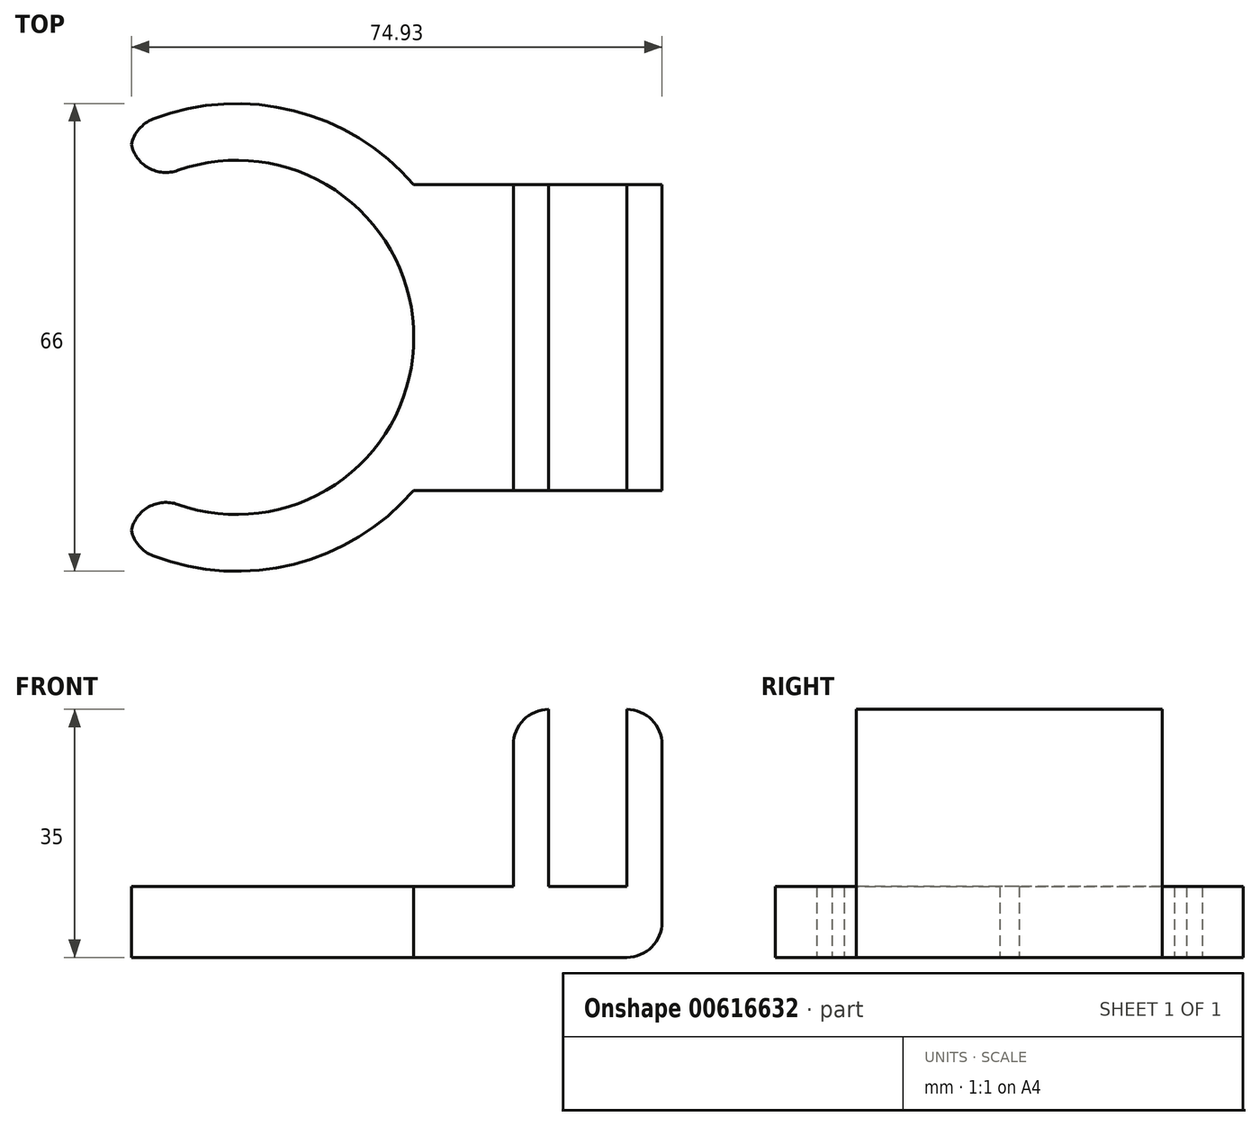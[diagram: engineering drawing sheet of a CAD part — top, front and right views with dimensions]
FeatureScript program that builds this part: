
annotation { "Feature Type Name" : "Feature", "Feature Type Description" : "" }
export const myFeature = defineFeature(function(context is Context, id is Id, definition is map)
    precondition{}
    {
        {
            var Q0;
            Q0=qCreatedBy(makeId("Top.planeOp"),FACE);
            var sketch = newSketch(context, id + "F0", { "sketchPlane" : qUnion([Q0])});
            skArc(sketch, "E0", {"start": v(-47, -20) * mm, "mid": v(-7, 0) * mm, "end": v(-47, 20) * mm});
            skArc(sketch, "E1", {"start": v(-47, -29.4) * mm, "mid": v(1, 0) * mm, "end": v(-47, 29.4) * mm});
            skLineSegment(sketch, "E2", {"start": v(-47, 29.4) * mm, "end": v(-47, 20) * mm});
            skLineSegment(sketch, "E3.trimOffspring", {"start": v(-47, -20) * mm, "end": v(-47, -29.4) * mm});
            skLineSegment(sketch, "E4.bottom", {"start": v(-7.04, 21.58) * mm, "end": v(7.04, 21.58) * mm});
            skLineSegment(sketch, "E4.top", {"start": v(-7.04, -21.58) * mm, "end": v(7.04, -21.58) * mm});
            skLineSegment(sketch, "E4.left", {"start": v(-7.04, 21.58) * mm, "end": v(-7.04, -21.58) * mm});
            skLineSegment(sketch, "E4.right", {"start": v(7.04, 21.58) * mm, "end": v(7.04, -21.58) * mm});
            skPoint(sketch, "E4.middle", {"position": v(0, 0) * mm});
            skLineSegment(sketch, "E5.bottom", {"start": v(7.04, 21.58) * mm, "end": v(12.04, 21.58) * mm});
            skLineSegment(sketch, "E5.top", {"start": v(7.04, -21.58) * mm, "end": v(12.04, -21.58) * mm});
            skLineSegment(sketch, "E5.right", {"start": v(12.04, 21.58) * mm, "end": v(12.04, -21.58) * mm});
            skLineSegment(sketch, "E6.bottom", {"start": v(12.04, 21.58) * mm, "end": v(23.04, 21.58) * mm});
            skLineSegment(sketch, "E6.top", {"start": v(12.04, -21.58) * mm, "end": v(23.04, -21.58) * mm});
            skLineSegment(sketch, "E6.right", {"start": v(23.04, 21.58) * mm, "end": v(23.04, -21.58) * mm});
            skLineSegment(sketch, "E7.bottom", {"start": v(23.04, 21.58) * mm, "end": v(28.04, 21.58) * mm});
            skLineSegment(sketch, "E7.top", {"start": v(23.04, -21.58) * mm, "end": v(28.04, -21.58) * mm});
            skLineSegment(sketch, "E7.right", {"start": v(28.04, 21.58) * mm, "end": v(28.04, -21.58) * mm});
            skSolve(sketch);
        }
        {
            var Q0;
            Q0=qSketchRegion(id+"F0",true);
            var Q1;
            {var subQ0=sQuery(id+"F0.wireOp",EDGE,"45a05517-1ebe-4f36-a2c0-a8144c21bbce1.MirrorCS");var subQ1=sQuery(id+"F0.wireOp",EDGE,"E1");var subQ2=makeQuery(id+"F0.imprint","INTERSECT",VERTEX,{"disambiguationData":[OD(0.0)],"derivedFrom":[subQ1,subQ0]});Q1=makeQuery(id+"F0.imprint","IMPRINT",FACE,{"disambiguationData":[TD([[makeQuery(id+"F0.imprint","IMPRINT",EDGE,{"disambiguationData":[TD([[subQ2,-1.0]])],"derivedFrom":subQ1}),1.0]])]});}
            extrude(context, id + "F1", {"entities" : qUnion([Q0, Q1]), "depth" : 5 * mm, "offsetDistance" : 25 * mm, "hasSecondDirection" : true, "secondDirectionOppositeDirection" : true, "secondDirectionDepth" : 5 * mm});
        }
        {
            var Q0;
            Q0=makeQuery(id+"F1.opExtrude","SWEPT_EDGE",EDGE,{"disambiguationData":[OSD([sQuery(id+"F0.wireOp",EDGE,"E0"),sQuery(id+"F0.wireOp",EDGE,"E2")])]});
            var Q1;
            Q1=makeQuery(id+"F1.opExtrude","SWEPT_EDGE",EDGE,{"disambiguationData":[OSD([sQuery(id+"F0.wireOp",EDGE,"E1"),sQuery(id+"F0.wireOp",EDGE,"E3.trimOffspring")])]});
            var Q2;
            Q2=makeQuery(id+"F1.opExtrude","SWEPT_EDGE",EDGE,{"disambiguationData":[OSD([sQuery(id+"F0.wireOp",EDGE,"E0"),sQuery(id+"F0.wireOp",EDGE,"E3.trimOffspring")])]});
            var Q3;
            Q3=makeQuery(id+"F1.opExtrude","SWEPT_EDGE",EDGE,{"disambiguationData":[OSD([sQuery(id+"F0.wireOp",EDGE,"E1"),sQuery(id+"F0.wireOp",EDGE,"E2")])]});
            var Q4;
            Q4=makeQuery(id+"F1.opExtrude","SWEPT_EDGE",EDGE,{"disambiguationData":[OSD([sQuery(id+"F0.wireOp",EDGE,"45a05517-1ebe-4f36-a2c0-a8144c21bbce1.MirrorCS"),sQuery(id+"F0.wireOp",EDGE,"45a05517-1ebe-4f36-a2c0-a8144c21bbce3.MirrorCS")])]});
            var Q5;
            Q5=makeQuery(id+"F1.opExtrude","SWEPT_EDGE",EDGE,{"disambiguationData":[OSD([sQuery(id+"F0.wireOp",EDGE,"45a05517-1ebe-4f36-a2c0-a8144c21bbce0.MirrorCS"),sQuery(id+"F0.wireOp",EDGE,"45a05517-1ebe-4f36-a2c0-a8144c21bbce3.MirrorCS")])]});
            var Q6;
            Q6=makeQuery(id+"F1.opExtrude","SWEPT_EDGE",EDGE,{"disambiguationData":[OSD([sQuery(id+"F0.wireOp",EDGE,"45a05517-1ebe-4f36-a2c0-a8144c21bbce0.MirrorCS"),sQuery(id+"F0.wireOp",EDGE,"45a05517-1ebe-4f36-a2c0-a8144c21bbce2.MirrorCS")])]});
            var Q7;
            Q7=makeQuery(id+"F1.opExtrude","SWEPT_EDGE",EDGE,{"disambiguationData":[OSD([sQuery(id+"F0.wireOp",EDGE,"45a05517-1ebe-4f36-a2c0-a8144c21bbce1.MirrorCS"),sQuery(id+"F0.wireOp",EDGE,"45a05517-1ebe-4f36-a2c0-a8144c21bbce2.MirrorCS")])]});
            fillet(context, id + "F2", {"entities" : qUnion([Q0, Q1, Q2, Q3, Q4, Q5, Q6, Q7]), "radius" : 5 * mm, "tangentPropagation" : true, "allowEdgeOverflow" : false});
        }
        {
            var Q0;
            Q0=makeQuery(id+"F1.opExtrude","CAP_FACE",FACE,{"disambiguationData":[OSD([sQuery(id+"F0.wireOp",EDGE,"E0"),sQuery(id+"F0.wireOp",EDGE,"E1"),sQuery(id+"F0.wireOp",EDGE,"E2"),sQuery(id+"F0.wireOp",EDGE,"E3.trimOffspring"),sQuery(id+"F0.wireOp",EDGE,"E4.bottom"),sQuery(id+"F0.wireOp",EDGE,"E4.top"),sQuery(id+"F0.wireOp",EDGE,"E4.left"),sQuery(id+"F0.wireOp",EDGE,"E5.bottom"),sQuery(id+"F0.wireOp",EDGE,"E5.top"),sQuery(id+"F0.wireOp",EDGE,"E6.bottom"),sQuery(id+"F0.wireOp",EDGE,"E6.top"),sQuery(id+"F0.wireOp",EDGE,"E7.bottom"),sQuery(id+"F0.wireOp",EDGE,"E7.top"),sQuery(id+"F0.wireOp",EDGE,"E7.right")])],"isStart":false});
            var sketch = newSketch(context, id + "F3", { "sketchPlane" : qUnion([Q0])});
            skLineSegment(sketch, "E8.0", {"start": v(7.04, 21.58) * mm, "end": v(7.04, -21.58) * mm});
            skLineSegment(sketch, "E9.0", {"start": v(12.04, 21.58) * mm, "end": v(12.04, -21.58) * mm});
            skLineSegment(sketch, "E10.0", {"start": v(23.04, 21.58) * mm, "end": v(23.04, -21.58) * mm});
            skLineSegment(sketch, "E11.0", {"start": v(28.04, 21.58) * mm, "end": v(28.04, -21.58) * mm});
            skLineSegment(sketch, "E12.bottom", {"start": v(7.04, 21.58) * mm, "end": v(12.04, 21.58) * mm});
            skLineSegment(sketch, "E12.top", {"start": v(7.04, -21.58) * mm, "end": v(12.04, -21.58) * mm});
            skLineSegment(sketch, "E13.bottom", {"start": v(23.04, 21.58) * mm, "end": v(28.04, 21.58) * mm});
            skLineSegment(sketch, "E13.top", {"start": v(23.04, -21.58) * mm, "end": v(28.04, -21.58) * mm});
            skSolve(sketch);
        }
        {
            var Q0;
            Q0 = qSketchRegion(id + "F3", true);
            extrude(context, id + "F4", {"entities" : qUnion([Q0]), "operationType" : NewBodyOperationType.ADD, "depth" : 25 * mm, "offsetDistance" : 25 * mm});
        }
        {
            var Q0;
            Q0=makeQuery(id+"F4.opExtrude","CAP_EDGE",EDGE,{"disambiguationData":[OSD([sQuery(id+"F3.wireOp",EDGE,"E8.0")])],"isStart":true});
            var Q1;
            Q1=makeQuery(id+"F4.opExtrude","CAP_EDGE",EDGE,{"disambiguationData":[OSD([sQuery(id+"F3.wireOp",EDGE,"E8.0")])],"isStart":false});
            var Q2;
            Q2=makeQuery(id+"F4.opExtrude","CAP_EDGE",EDGE,{"disambiguationData":[OSD([sQuery(id+"F3.wireOp",EDGE,"E11.0")])],"isStart":false});
            var Q3;
            Q3=makeQuery(id+"F1.opExtrude","CAP_EDGE",EDGE,{"disambiguationData":[OSD([sQuery(id+"F0.wireOp",EDGE,"E7.right")])],"isStart":true});
            fillet(context, id + "F5", {"entities" : qUnion([Q0, Q1, Q2, Q3]), "radius" : 5 * mm, "tangentPropagation" : true, "allowEdgeOverflow" : false});
        }
    });
